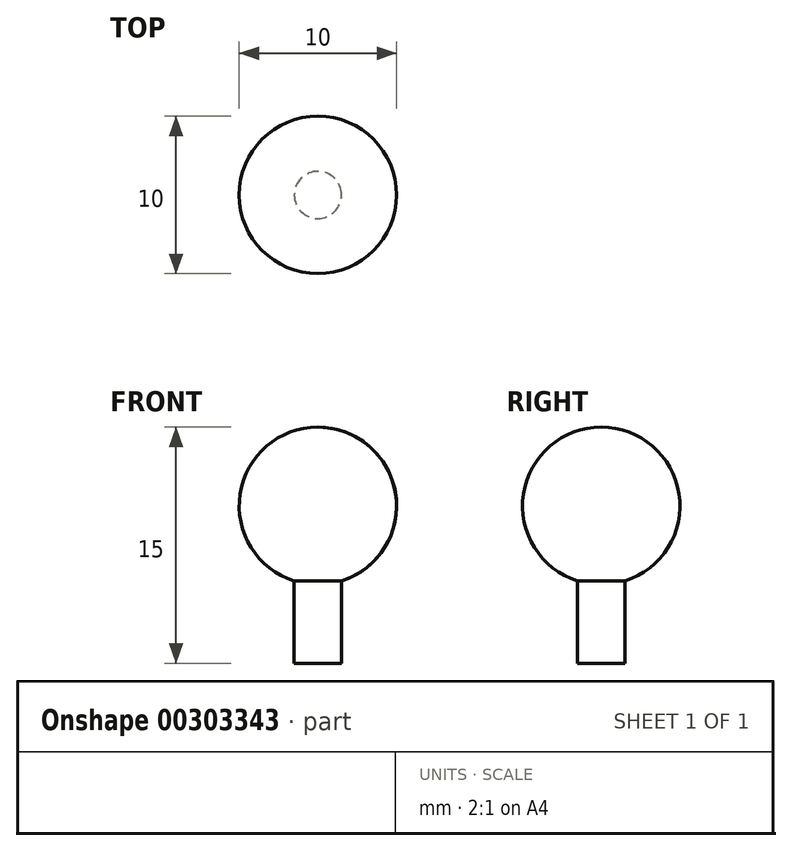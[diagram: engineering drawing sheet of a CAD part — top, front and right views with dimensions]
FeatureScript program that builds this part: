
annotation { "Feature Type Name" : "Feature", "Feature Type Description" : "" }
export const myFeature = defineFeature(function(context is Context, id is Id, definition is map)
    precondition{}
    {
        {
            var Q0;
            Q0=qCreatedBy(makeId("Front.planeOp"),FACE);
            var sketch = newSketch(context, id + "F0", { "sketchPlane" : qUnion([Q0])});
            skArc(sketch, "E0", {"start": v(1.5, -4.77) * mm, "mid": v(4.94, 0.76) * mm, "end": v(0, 5) * mm});
            skLineSegment(sketch, "E1.top", {"start": v(0, -10) * mm, "end": v(1.5, -10) * mm});
            skLineSegment(sketch, "E1.right", {"start": v(1.5, -4.77) * mm, "end": v(1.5, -10) * mm});
            skPoint(sketch, "E2.orphan", {"position": v(-1.5, 10) * mm});
            skPoint(sketch, "E3.orphan", {"position": v(1.5, 10) * mm});
            skLineSegment(sketch, "E4", {"start": v(0, 5) * mm, "end": v(0, -10) * mm});
            skPoint(sketch, "E5.orphan", {"position": v(-1.5, -10) * mm});
            skSolve(sketch);
        }
        {
            var Q0;
            Q0=makeQuery(id+"F0.imprint","IMPRINT",FACE,{"disambiguationData":[TD([[makeQuery(id+"F0.imprint","IMPRINT",EDGE,{"derivedFrom":sQuery(id+"F0.wireOp",EDGE,"E0")}),1.0]])]});
            var Q1;
            Q1=sQuery(id+"F0.wireOp",EDGE,"E4");
            revolve(context, id + "F1", {"entities" : qUnion([Q0]), "axis" : qUnion([Q1]), "revolveType" : RevolveType.FULL});
        }
    });
